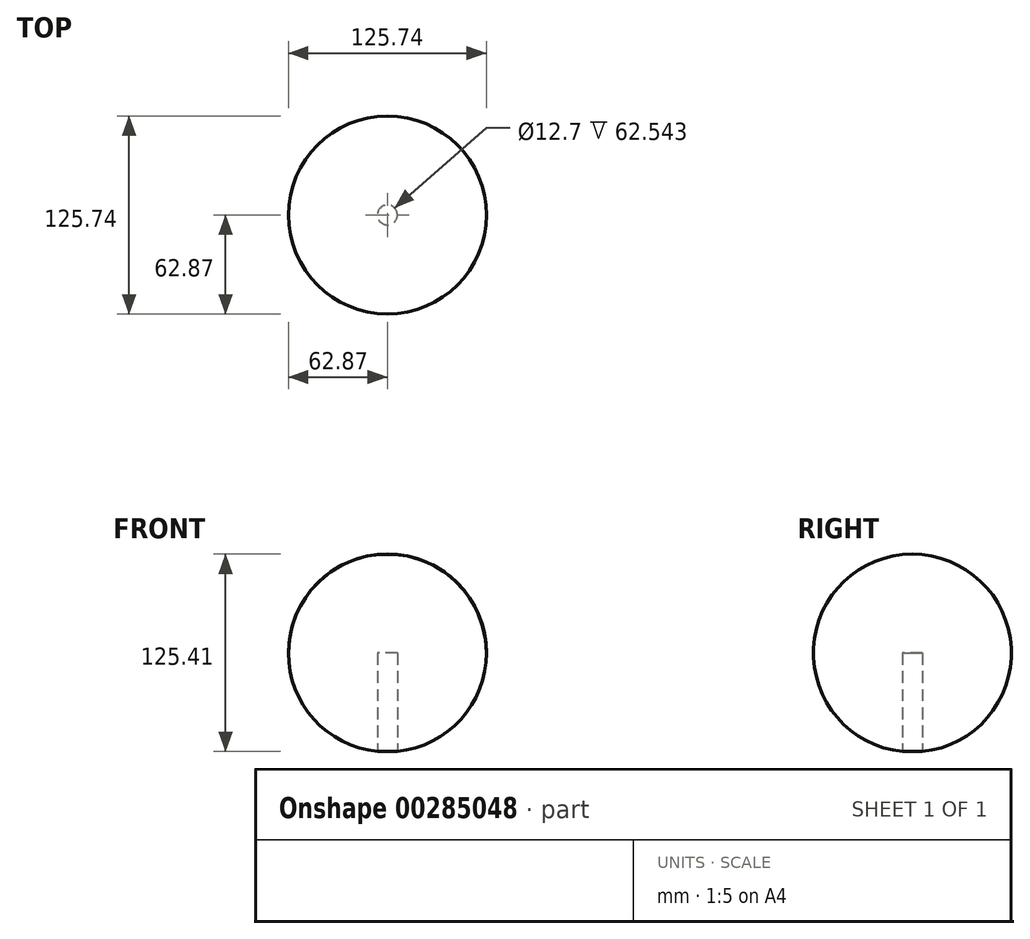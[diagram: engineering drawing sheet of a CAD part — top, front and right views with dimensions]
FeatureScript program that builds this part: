
annotation { "Feature Type Name" : "Feature", "Feature Type Description" : "" }
export const myFeature = defineFeature(function(context is Context, id is Id, definition is map)
    precondition{}
    {
        {
            var Q0;
            Q0=qCreatedBy(makeId("Front.planeOp"),FACE);
            var sketch = newSketch(context, id + "F0", { "sketchPlane" : qUnion([Q0])});
            skArc(sketch, "E0", {"start": v(62.87, 0) * mm, "mid": v(0, 62.87) * mm, "end": v(-62.87, 0) * mm});
            skLineSegment(sketch, "E1", {"start": v(-62.87, 0) * mm, "end": v(62.87, 0) * mm});
            skSolve(sketch);
        }
        {
            var Q0;
            Q0=makeQuery(id+"F0.imprint","IMPRINT",FACE,{"disambiguationData":[TD([[makeQuery(id+"F0.imprint","IMPRINT",EDGE,{"derivedFrom":sQuery(id+"F0.wireOp",EDGE,"E0")}),1.0]])]});
            var Q1;
            Q1=sQuery(id+"F0.wireOp",EDGE,"E1");
            revolve(context, id + "F1", {"entities" : qUnion([Q0]), "axis" : qUnion([Q1]), "revolveType" : RevolveType.FULL});
        }
        {
            var Q0;
            Q0=qCreatedBy(makeId("Top.planeOp"),FACE);
            cPlane(context, id + "F2", {"entities" : qUnion([Q0]), "cplaneType" : CPlaneType.OFFSET, "offset" : 76.2 * mm, "oppositeDirection" : true, "width" : 152.4 * mm, "height" : 152.4 * mm});
        }
        {
            var Q0;
            Q0=qCreatedBy(id+"F2.planeOp",FACE);
            var sketch = newSketch(context, id + "F3", { "sketchPlane" : qUnion([Q0])});
            skCircle(sketch, "E2", {"center": v(0, 0) * mm, "radius": 6.35 * mm});
            skSolve(sketch);
        }
        {
            var Q0;
            Q0=makeQuery(id+"F3.imprint","IMPRINT",FACE,{"disambiguationData":[TD([[makeQuery(id+"F3.imprint","IMPRINT",EDGE,{"derivedFrom":sQuery(id+"F3.wireOp",EDGE,"E2")}),1.0]])]});
            extrude(context, id + "F4", {"entities" : qUnion([Q0]), "operationType" : NewBodyOperationType.REMOVE, "depth" : 76.2 * mm});
        }
    });
